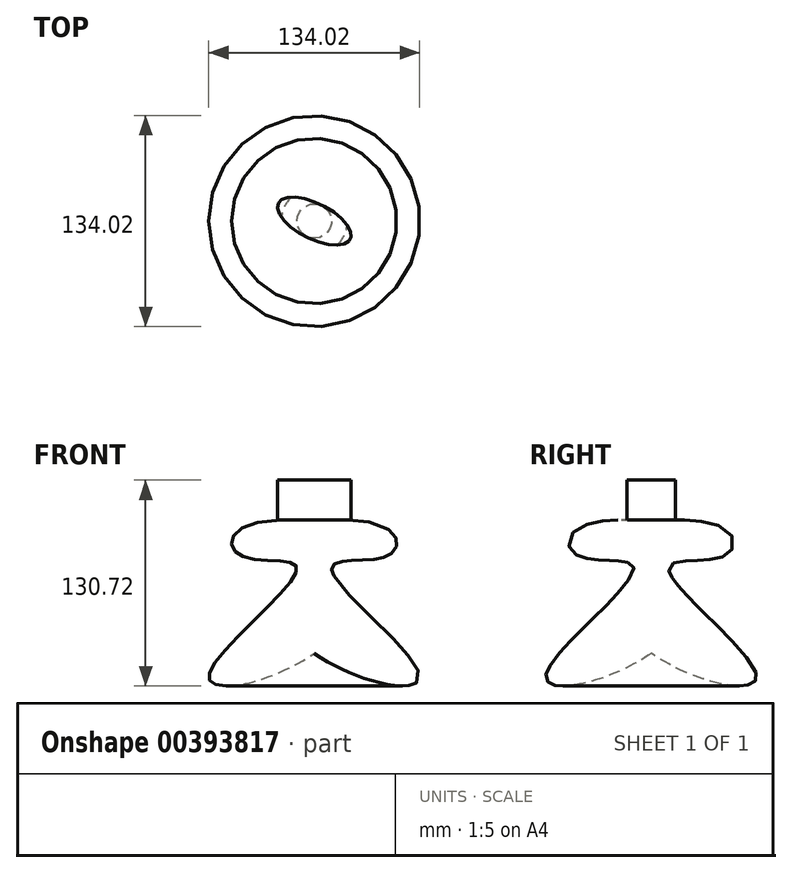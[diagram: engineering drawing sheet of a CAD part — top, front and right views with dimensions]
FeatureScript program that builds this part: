
annotation { "Feature Type Name" : "Feature", "Feature Type Description" : "" }
export const myFeature = defineFeature(function(context is Context, id is Id, definition is map)
    precondition{}
    {
        {
            var Q0;
            Q0=qCreatedBy(makeId("Front.planeOp"),FACE);
            var sketch = newSketch(context, id + "F0", { "sketchPlane" : qUnion([Q0])});
            skLineSegment(sketch, "E0", {"start": v(37.51, 64.42) * mm, "end": v(37.51, -37.2) * mm});
            skFitSpline(sketch, "E1", {"points": [v(16.48, 64.42) * mm, v(-10.14, 42.35) * mm, v(26.55, 34.1) * mm, v(-29.45, -34.1) * mm, v(37.51, -20.19) * mm], "startDerivative": vector(-495.4, 0) * mm, "endDerivative": vector(311.79, 216.39) * mm});
            skLineSegment(sketch, "E2", {"start": v(37.51, 64.42) * mm, "end": v(16.48, 64.42) * mm});
            skSolve(sketch);
        }
        {
            var Q0;
            Q0 = qSketchRegion(id + "F0", true);
            var Q1;
            Q1=sQuery(id+"F0.wireOp",EDGE,"E0");
            revolve(context, id + "F1", {"entities" : qUnion([Q0]), "axis" : qUnion([Q1]), "revolveType" : RevolveType.FULL});
        }
        {
            var Q0;
            Q0=makeQuery(id+"F1.opRevolve","SWEPT_FACE",FACE,{"disambiguationData":[OSD([sQuery(id+"F0.wireOp",EDGE,"E2")])]});
            var sketch = newSketch(context, id + "F2", { "sketchPlane" : qUnion([Q0])});
            skEllipse(sketch, "E3", {"center": v(37.51, 0) * mm, "majorRadius": 25.56 * mm, "minorRadius": 11.24 * mm, "majorAxis": v(-0.9, 0.45)});
            skSolve(sketch);
        }
        {
            var Q0;
            Q0 = qSketchRegion(id + "F2", true);
            var Q1;
            Q1=makeQuery(id+"F1.opRevolve","SWEPT_BODY",BODY,{"disambiguationData":[OSD([sQuery(id+"F0.wireOp",EDGE,"E0"),sQuery(id+"F0.wireOp",EDGE,"E1"),sQuery(id+"F0.wireOp",EDGE,"E2")])]});
            extrude(context, id + "F3", {"entities" : qUnion([Q0]), "operationType" : NewBodyOperationType.ADD, "depth" : 25.4 * mm});
        }
    });
